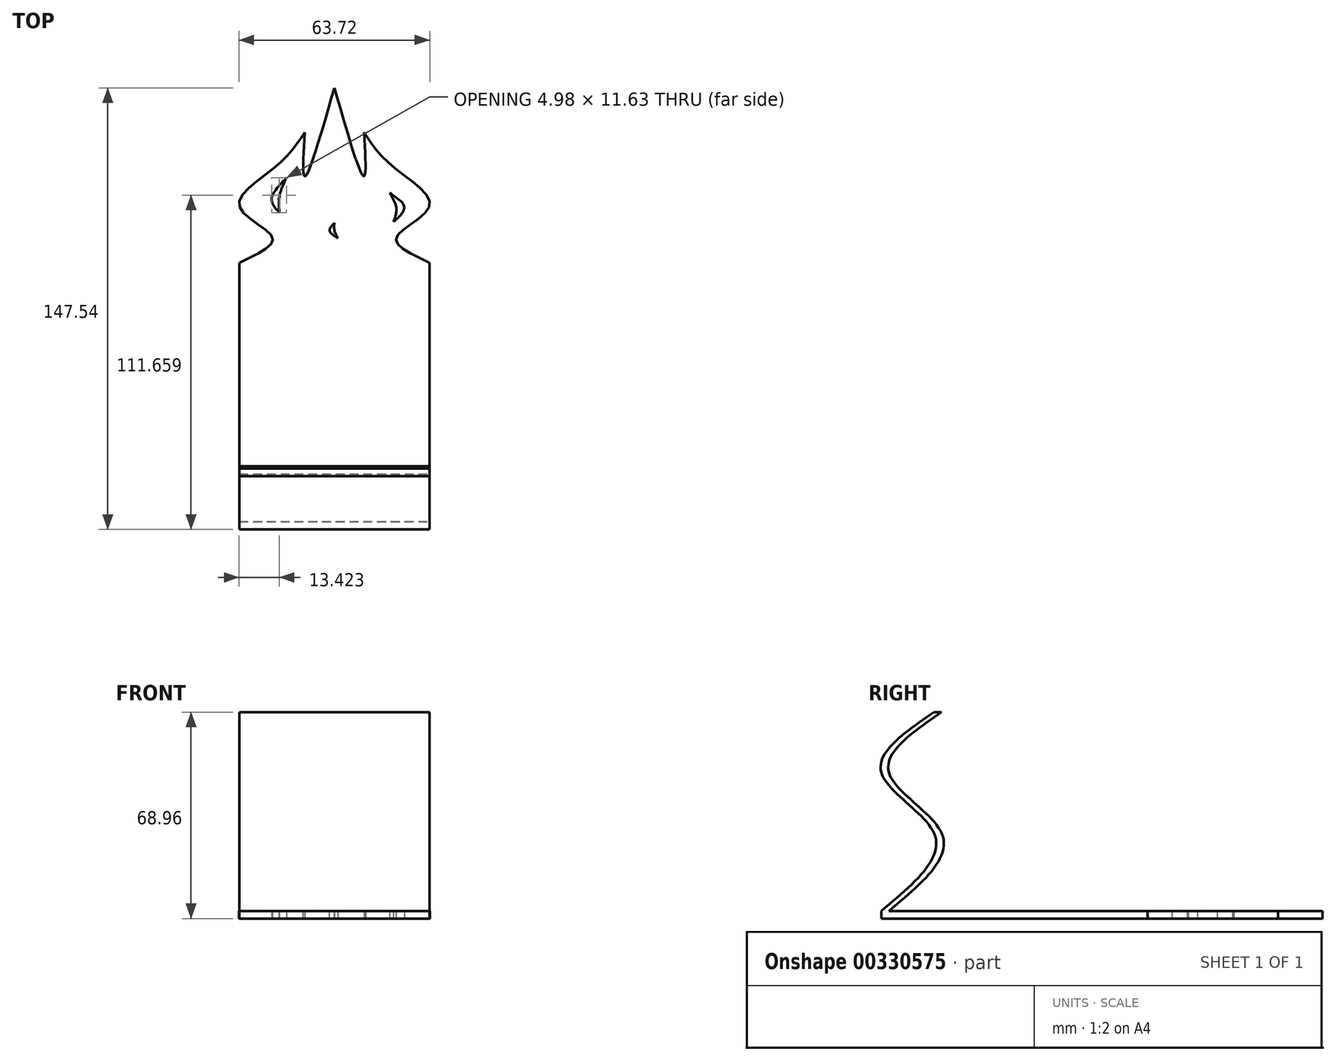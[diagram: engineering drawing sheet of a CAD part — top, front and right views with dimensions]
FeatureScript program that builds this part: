
annotation { "Feature Type Name" : "Feature", "Feature Type Description" : "" }
export const myFeature = defineFeature(function(context is Context, id is Id, definition is map)
    precondition{}
    {
        {
            var Q0;
            Q0=qCreatedBy(makeId("Top.planeOp"),FACE);
            var sketch = newSketch(context, id + "F0", { "sketchPlane" : qUnion([Q0])});
            skLineSegment(sketch, "E0.bottom", {"start": v(31.75, -83.68) * mm, "end": v(-31.75, -83.68) * mm});
            skLineSegment(sketch, "E0.left", {"start": v(31.75, -83.68) * mm, "end": v(31.75, 5.22) * mm});
            skLineSegment(sketch, "E0.right", {"start": v(-31.75, -83.68) * mm, "end": v(-31.75, 5.22) * mm});
            skPoint(sketch, "E0.middle", {"position": v(0, -39.23) * mm});
            skFitSpline(sketch, "E1", {"points": [v(-31.75, 5.22) * mm, v(-20.7, 13.6) * mm, v(-31.75, 24.17) * mm, v(-19.3, 37.56) * mm, v(-9.88, 48.77) * mm], "startDerivative": vector(76.58, 37.95) * mm, "endDerivative": vector(29.11, 44.3) * mm});
            skFitSpline(sketch, "E2.MirrorCS", {"points": [v(31.75, 5.22) * mm, v(20.7, 13.6) * mm, v(31.75, 24.17) * mm, v(19.3, 37.56) * mm, v(9.88, 48.77) * mm], "startDerivative": vector(-76.58, 37.95) * mm, "endDerivative": vector(-29.11, 44.3) * mm});
            skFitSpline(sketch, "E3", {"points": [v(-9.88, 48.77) * mm, v(-9.88, 34.11) * mm, v(0, 63.64) * mm], "startDerivative": vector(-3.4, -53.5) * mm, "endDerivative": vector(21.6, 75.25) * mm});
            skFitSpline(sketch, "E4.MirrorCS", {"points": [v(9.88, 48.77) * mm, v(9.88, 34.11) * mm, v(0, 63.64) * mm], "startDerivative": vector(3.4, -53.5) * mm, "endDerivative": vector(-21.6, 75.25) * mm});
            skFitSpline(sketch, "E5", {"points": [v(-18.36, 21.94) * mm, v(-20.98, 26.48) * mm, v(-15.95, 33.57) * mm], "startDerivative": vector(-9.26, 9.9) * mm, "endDerivative": vector(13.14, 13.22) * mm});
            skFitSpline(sketch, "E6", {"points": [v(-15.95, 33.57) * mm, v(-18.3, 27.68) * mm, v(-18.36, 21.94) * mm], "startDerivative": vector(-5.76, -11.42) * mm, "endDerivative": vector(1, -11.84) * mm});
            skFitSpline(sketch, "E7", {"points": [v(18.47, 28.48) * mm, v(20.65, 23.84) * mm, v(20.4, 20.85) * mm, v(19.76, 18.82) * mm], "startDerivative": vector(6.93, -11.57) * mm, "endDerivative": vector(-2.49, -7.24) * mm});
            skFitSpline(sketch, "E8", {"points": [v(18.47, 28.48) * mm, v(23.33, 23.8) * mm, v(19.76, 18.82) * mm], "startDerivative": vector(13.8, -8.9) * mm, "endDerivative": vector(-11.43, -10.44) * mm});
            skFitSpline(sketch, "E9", {"points": [v(0, 18.44) * mm, v(-1.58, 15.96) * mm, v(1.18, 13.4) * mm], "startDerivative": vector(-5.37, -5.4) * mm, "endDerivative": vector(7.46, -4.7) * mm});
            skFitSpline(sketch, "E10", {"points": [v(0, 18.44) * mm, v(0, 16.1) * mm, v(1.18, 13.4) * mm], "startDerivative": vector(-0.53, -4.93) * mm, "endDerivative": vector(2.82, -5.14) * mm});
            skSolve(sketch);
        }
        {
            var Q0;
            Q0=makeQuery(id+"F0.imprint","IMPRINT",FACE,{"disambiguationData":[TD([[makeQuery(id+"F0.imprint","IMPRINT",EDGE,{"derivedFrom":sQuery(id+"F0.wireOp",EDGE,"E0.bottom")}),-1.0]])]});
            extrude(context, id + "F1", {"entities" : qUnion([Q0]), "depth" : 2.54 * mm});
        }
        {
            var Q0;
            Q0=makeQuery(id+"F1.opExtrude","SWEPT_FACE",FACE,{"disambiguationData":[OSD([sQuery(id+"F0.wireOp",EDGE,"E0.left")])]});
            var sketch = newSketch(context, id + "F2", { "sketchPlane" : qUnion([Q0])});
            skFitSpline(sketch, "E11", {"points": [v(-83.68, 2.54) * mm, v(-65.65, 27.44) * mm, v(-83.68, 48.88) * mm, v(-66.05, 68.96) * mm], "startDerivative": vector(88.66, 73.63) * mm, "endDerivative": vector(90.21, 61.94) * mm});
            skLineSegment(sketch, "E12", {"start": v(-63.5, 68.96) * mm, "end": v(-66.05, 68.96) * mm});
            skLineSegment(sketch, "E13", {"start": v(-81.14, 48.88) * mm, "end": v(-83.68, 48.88) * mm});
            skLineSegment(sketch, "E14", {"start": v(-63.1, 27.44) * mm, "end": v(-65.65, 27.44) * mm});
            skLineSegment(sketch, "E15", {"start": v(-83.68, 2.54) * mm, "end": v(-81.14, 2.54) * mm});
            skFitSpline(sketch, "E16", {"points": [v(-63.5, 68.96) * mm, v(-81.14, 48.88) * mm, v(-63.1, 27.44) * mm, v(-81.14, 2.54) * mm], "startDerivative": vector(-90.21, -61.94) * mm, "endDerivative": vector(-88.66, -73.63) * mm});
            skSolve(sketch);
        }
        {
            var Q0;
            {var subQ0=sQuery(id+"F2.wireOp",EDGE,"E13");Q0=makeQuery(id+"F2.imprint","IMPRINT",FACE,{"disambiguationData":[TD([[makeQuery(id+"F2.imprint","IMPRINT",EDGE,{"derivedFrom":subQ0}),1.0]])]});}
            var Q1;
            {var subQ0=sQuery(id+"F2.wireOp",EDGE,"E12");Q1=makeQuery(id+"F2.imprint","IMPRINT",FACE,{"disambiguationData":[TD([[makeQuery(id+"F2.imprint","IMPRINT",EDGE,{"derivedFrom":subQ0}),1.0]])]});}
            var Q2;
            {var subQ3=sQuery(id+"F2.wireOp",EDGE,"E14");Q2=makeQuery(id+"F2.imprint","IMPRINT",FACE,{"disambiguationData":[TD([[makeQuery(id+"F2.imprint","IMPRINT",EDGE,{"derivedFrom":subQ3}),1.0]])]});}
            extrude(context, id + "F3", {"entities" : qUnion([Q0, Q1, Q2]), "operationType" : NewBodyOperationType.ADD, "oppositeDirection" : true, "depth" : 63.5 * mm});
        }
    });
